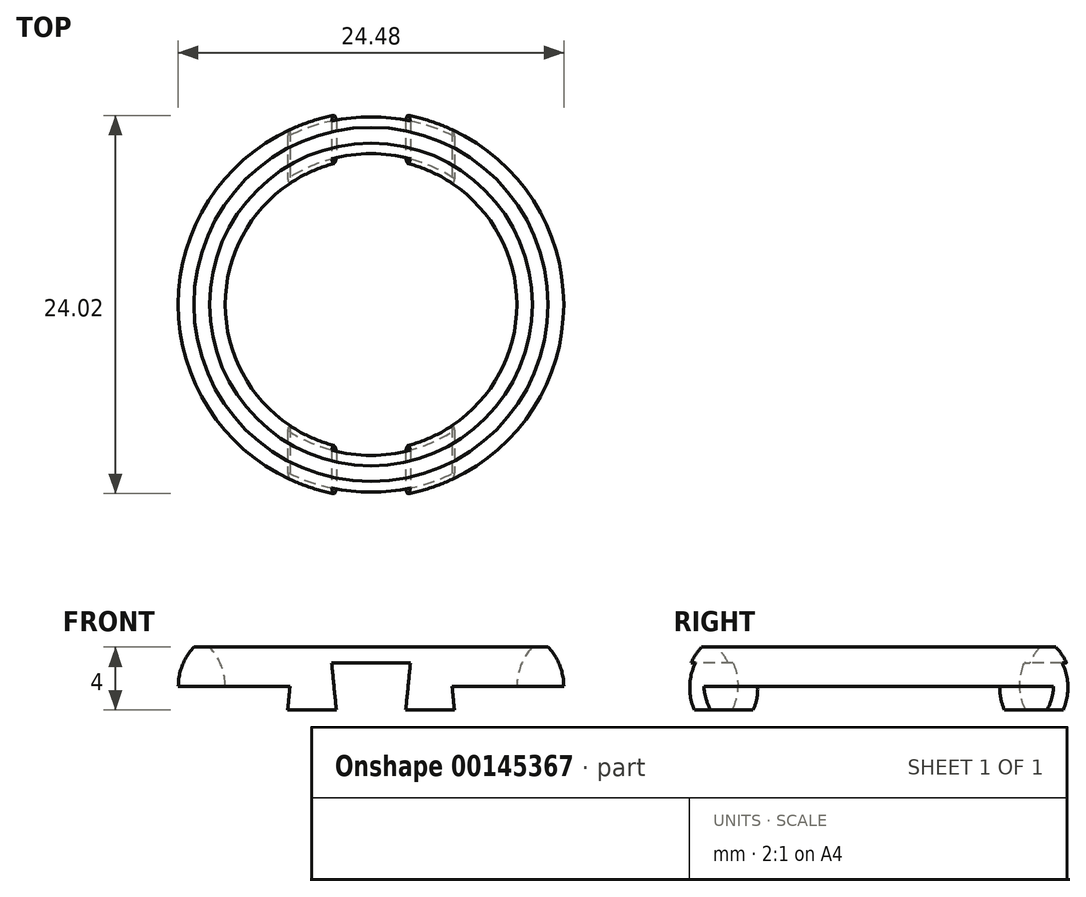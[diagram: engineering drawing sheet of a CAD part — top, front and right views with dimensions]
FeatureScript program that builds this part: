
annotation { "Feature Type Name" : "Feature", "Feature Type Description" : "" }
export const myFeature = defineFeature(function(context is Context, id is Id, definition is map)
    precondition{}
    {
        {
            var Q0;
            Q0=qCreatedBy(makeId("Front.planeOp"),FACE);
            var sketch = newSketch(context, id + "F0", { "sketchPlane" : qUnion([Q0])});
            skLineSegment(sketch, "E0", {"start": v(0, 0) * mm, "end": v(0, 5) * mm});
            skArc(sketch, "E1", {"start": v(-10.25, 0) * mm, "mid": v(-9.26, 2.5) * mm, "end": v(-10.25, 5) * mm});
            skLineSegment(sketch, "E2", {"start": v(-11.25, 5) * mm, "end": v(-10.25, 5) * mm});
            skLineSegment(sketch, "E3", {"start": v(-11.25, 0) * mm, "end": v(-10.25, 0) * mm});
            skArc(sketch, "E4", {"start": v(-11.25, 5) * mm, "mid": v(-12.24, 2.5) * mm, "end": v(-11.25, 0) * mm});
            skPoint(sketch, "E5.orphan", {"position": v(-12.25, 5) * mm});
            skPoint(sketch, "E6.orphan", {"position": v(-12.25, 0) * mm});
            skSolve(sketch);
        }
        {
            var Q0;
            Q0=qSketchRegion(id+"F0",true);
            var Q1;
            Q1=sQuery(id+"F0.wireOp",EDGE,"E0");
            revolve(context, id + "F1", {"entities" : qUnion([Q0]), "axis" : qUnion([Q1]), "revolveType" : RevolveType.FULL});
        }
        {
            var Q0;
            Q0=qCreatedBy(makeId("Front.planeOp"),FACE);
            var sketch = newSketch(context, id + "F2", { "sketchPlane" : qUnion([Q0])});
            skLineSegment(sketch, "E7", {"start": v(-12.26, 2.5) * mm, "end": v(-5.15, 2.5) * mm});
            skLineSegment(sketch, "E8", {"start": v(0, 0) * mm, "end": v(0, 4.5) * mm});
            skLineSegment(sketch, "E9", {"start": v(0, 2.5) * mm, "end": v(0, 3.83) * mm});
            skLineSegment(sketch, "E10", {"start": v(0, 2.5) * mm, "end": v(0, 3.47) * mm});
            skLineSegment(sketch, "E11", {"start": v(0, 2.5) * mm, "end": v(0, 4.5) * mm});
            skLineSegment(sketch, "E12", {"start": v(-2.5, 4) * mm, "end": v(-2.2, 1) * mm});
            skLineSegment(sketch, "E13.0", {"start": v(-5.3, 1) * mm, "end": v(-2.2, 1) * mm});
            skLineSegment(sketch, "E14.0.MirrorCS", {"start": v(-5.15, 2.5) * mm, "end": v(-5.3, 1) * mm});
            skLineSegment(sketch, "E15.trimOffspring", {"start": v(-2.5, 4) * mm, "end": v(0, 4) * mm});
            skLineSegment(sketch, "E16.0.MirrorCS", {"start": v(12.26, 2.5) * mm, "end": v(5.15, 2.5) * mm});
            skLineSegment(sketch, "E17.0.MirrorCS", {"start": v(5.15, 2.5) * mm, "end": v(5.3, 1) * mm});
            skLineSegment(sketch, "E18.0.MirrorCS", {"start": v(5.3, 1) * mm, "end": v(2.2, 1) * mm});
            skLineSegment(sketch, "E19.0.MirrorCS", {"start": v(2.5, 4) * mm, "end": v(2.2, 1) * mm});
            skLineSegment(sketch, "E20.0.MirrorCS", {"start": v(2.5, 4) * mm, "end": v(0, 4) * mm});
            skLineSegment(sketch, "E21", {"start": v(-12.26, -0.9) * mm, "end": v(12.26, -0.9) * mm});
            skLineSegment(sketch, "E22", {"start": v(-12.26, 2.5) * mm, "end": v(-12.26, -0.9) * mm});
            skLineSegment(sketch, "E23", {"start": v(12.26, 2.5) * mm, "end": v(12.26, -0.9) * mm});
            skPoint(sketch, "E24.orphan", {"position": v(-12.26, 5.63) * mm});
            skPoint(sketch, "E25.0.MirrorCS.end.orphan", {"position": v(12.26, 5.63) * mm});
            skPoint(sketch, "E26.0.MirrorCS.end.orphan", {"position": v(6.1, 2.5) * mm});
            skPoint(sketch, "E27.0.MirrorCS.start.orphan", {"position": v(6.25, 4) * mm});
            skPoint(sketch, "E28.orphan", {"position": v(5, 4) * mm});
            skPoint(sketch, "E29.0.end.orphan", {"position": v(-5, 4) * mm});
            skPoint(sketch, "E30.0.MirrorCS.end.orphan", {"position": v(-6.1, 2.5) * mm});
            skPoint(sketch, "E30.0.MirrorCS.start.orphan", {"position": v(-6.25, 4) * mm});
            skSolve(sketch);
        }
        {
            var Q0;
            Q0=qSketchRegion(id+"F2",true);
            extrude(context, id + "F3", {"entities" : qUnion([Q0]), "operationType" : NewBodyOperationType.REMOVE, "endBound" : BoundingType.SYMMETRIC, "oppositeDirection" : true, "depth" : 25 * mm});
        }
    });
